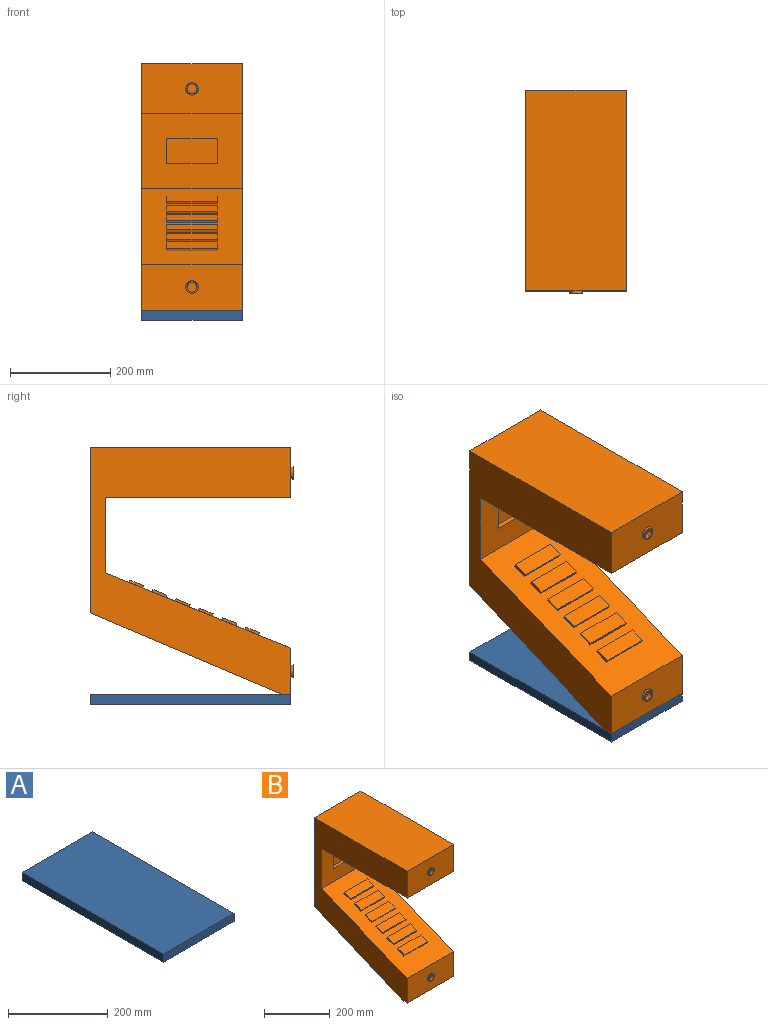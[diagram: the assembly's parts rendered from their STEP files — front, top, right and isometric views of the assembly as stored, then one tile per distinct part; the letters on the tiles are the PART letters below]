
ASSEMBLY  parts=2 mates=1
PART A: 6 faces, bbox 200x400x20 mm
  f0: plane 200x20mm, normal (0,1,0), area 4000mm2, adj f1,f3,f4,f5
  f1: plane 400x20mm, normal (-1,0,0), area 8000mm2, adj f0,f2,f4,f5
  f2: plane 200x20mm, normal (0,-1,0), area 4000mm2, adj f1,f3,f4,f5
  f3: plane 400x20mm, normal (1,0,0), area 8000mm2, adj f0,f2,f4,f5
  f4: plane 400x200mm, normal (0,0,1), area 80000mm2, adj f0,f1,f2,f3
  f5: plane 400x200mm, normal (0,0,-1), area 80000mm2, adj f0,f1,f2,f3
PART B: 59 faces, bbox 200x405x492.2 mm
  f0: plane 370x200mm, normal (0,-0.38,0.93), area 61849.9mm2, adj f1,f8,f9,f10,f21,f22,f23,f24
  f1: plane 200x92.23mm, normal (0,-1,0), area 17954.9mm2, adj f0,f2,f9,f10,f56
  f2: plane 200x18.28mm, normal (0,0,-1), area 3656.9mm2, adj f1,f3,f9,f10
  f3: plane 381.72x200mm, normal (0,0.39,-0.92), area 82951.8mm2, adj f2,f4,f9,f10
  f4: plane 330x200mm, normal (0,1,0), area 66000mm2, adj f3,f5,f9,f10
  f5: plane 400x200mm, normal (0,0,1), area 80000mm2, adj f4,f6,f9,f10
  f6: plane 200x100mm, normal (0,-1,0), area 19509.1mm2, adj f5,f7,f9,f10,f52
  f7: plane 370x200mm, normal (0,0,-1), area 40824mm2, adj f6,f8,f9,f10,f11,f12,f13,f14
  f8: plane 200x150mm, normal (0,-1,0), area 25000mm2, adj f0,f7,f9,f10,f16,f17,f18,f19
  f9: plane 492.23x400mm, normal (1,0,0), area 82679mm2, adj f0,f1,f2,f3,f4,f5,f6,f7
  f10: plane 492.23x400mm, normal (-1,0,0), area 82679mm2, adj f0,f1,f2,f3,f4,f5,f6,f7
  f11: plane 286x10mm, normal (1,0,0), area 2860mm2, adj f7,f12,f14,f15
  f12: plane 116x10mm, normal (0,-1,0), area 1160mm2, adj f7,f11,f13,f15
  f13: plane 286x10mm, normal (-1,0,0), area 2860mm2, adj f7,f12,f14,f15
  f14: plane 116x10mm, normal (0,1,0), area 1160mm2, adj f7,f11,f13,f15
  f15: plane 286x116mm, normal (0,0,-1), area 33176mm2, adj f11,f12,f13,f14
  f16: plane 50x10mm, normal (-1,0,0), area 500mm2, adj f8,f17,f19,f20
  f17: plane 100x10mm, normal (0,0,-1), area 1000mm2, adj f8,f16,f18,f20
  f18: plane 50x10mm, normal (1,0,0), area 500mm2, adj f8,f17,f19,f20
  f19: plane 100x10mm, normal (0,0,1), area 1000mm2, adj f8,f16,f18,f20
  f20: plane 100x50mm, normal (0,-1,0), area 5000mm2, adj f16,f17,f18,f19
  f21: plane 100x4.63mm, normal (0,0.93,0.38), area 500mm2, adj f0,f22,f24,f25
  f22: plane 29.68x15.91mm, normal (-1,0,0), area 150mm2, adj f0,f21,f23,f25
  f23: plane 100x4.63mm, normal (0,-0.93,-0.38), area 500mm2, adj f0,f22,f24,f25
  f24: plane 29.68x15.91mm, normal (1,0,0), area 150mm2, adj f0,f21,f23,f25
  f25: plane 100x27.8mm, normal (0,-0.38,0.93), area 3000mm2, adj f21,f22,f23,f24
  f26: plane 29.68x15.91mm, normal (-1,0,0), area 150mm2, adj f0,f27,f29,f30
  f27: plane 100x4.63mm, normal (0,-0.93,-0.38), area 500mm2, adj f0,f26,f28,f30
  f28: plane 29.68x15.91mm, normal (1,0,0), area 150mm2, adj f0,f27,f29,f30
  f29: plane 100x4.63mm, normal (0,0.93,0.38), area 500mm2, adj f0,f26,f28,f30
  f30: plane 100x27.8mm, normal (0,-0.38,0.93), area 3000mm2, adj f26,f27,f28,f29
  f31: plane 100x4.63mm, normal (0,-0.93,-0.38), area 500mm2, adj f0,f32,f34,f35
  f32: plane 29.68x15.91mm, normal (1,0,0), area 150mm2, adj f0,f31,f33,f35
  f33: plane 100x4.63mm, normal (0,0.93,0.38), area 500mm2, adj f0,f32,f34,f35
  f34: plane 29.68x15.91mm, normal (-1,0,0), area 150mm2, adj f0,f31,f33,f35
  f35: plane 100x27.8mm, normal (0,-0.38,0.93), area 3000mm2, adj f31,f32,f33,f34
  f36: plane 100x4.63mm, normal (0,-0.93,-0.38), area 500mm2, adj f0,f37,f39,f40
  f37: plane 29.68x15.91mm, normal (1,0,0), area 150mm2, adj f0,f36,f38,f40
  f38: plane 100x4.63mm, normal (0,0.93,0.38), area 500mm2, adj f0,f37,f39,f40
  f39: plane 29.68x15.91mm, normal (-1,0,0), area 150mm2, adj f0,f36,f38,f40
  f40: plane 100x27.8mm, normal (0,-0.38,0.93), area 3000mm2, adj f36,f37,f38,f39
  f41: plane 100x4.63mm, normal (0,-0.93,-0.38), area 500mm2, adj f0,f42,f44,f45
  f42: plane 29.68x15.91mm, normal (1,0,0), area 150mm2, adj f0,f41,f43,f45
  f43: plane 100x4.63mm, normal (0,0.93,0.38), area 500mm2, adj f0,f42,f44,f45
  f44: plane 29.68x15.91mm, normal (-1,0,0), area 150mm2, adj f0,f41,f43,f45
  f45: plane 100x27.8mm, normal (0,-0.38,0.93), area 3000mm2, adj f41,f42,f43,f44
  f46: plane 100x4.63mm, normal (0,-0.93,-0.38), area 500mm2, adj f0,f47,f49,f50
  f47: plane 29.68x15.91mm, normal (1,0,0), area 150mm2, adj f0,f46,f48,f50
  f48: plane 100x4.63mm, normal (0,0.93,0.38), area 500mm2, adj f0,f47,f49,f50
  f49: plane 29.68x15.91mm, normal (-1,0,0), area 150mm2, adj f0,f46,f48,f50
  f50: plane 100x27.8mm, normal (0,-0.38,0.93), area 3000mm2, adj f46,f47,f48,f49
  f51: cylinder r=10mm len=20mm, axis (0,-1,0), area 628.3mm2, adj f53,f54
  f52: cylinder r=12.5mm len=25mm, axis (0,-1,0), area 392.7mm2, adj f6,f53
  f53: plane 25x25mm, normal (0,-1,0), area 176.7mm2, adj f51,f52
  f54: plane 20x20mm, normal (0,-1,0), area 314.2mm2, adj f51
  f55: cylinder r=10mm len=20mm, axis (0,-1,0), area 628.3mm2, adj f57,f58
  f56: cylinder r=12.5mm len=25mm, axis (0,-1,0), area 392.7mm2, adj f1,f57
  f57: plane 25x25mm, normal (0,-1,0), area 176.7mm2, adj f55,f56
  f58: plane 20x20mm, normal (0,-1,0), area 314.2mm2, adj f55
PLACE A t=(-310.44,-34.5,103.44)mm
PLACE B t=(-410.18,-48.48,269.86)mm
MATE fastened A.f4 <-> B.f2  axis (0,0,1) through (-310.18,-135.3,123.44)mm
